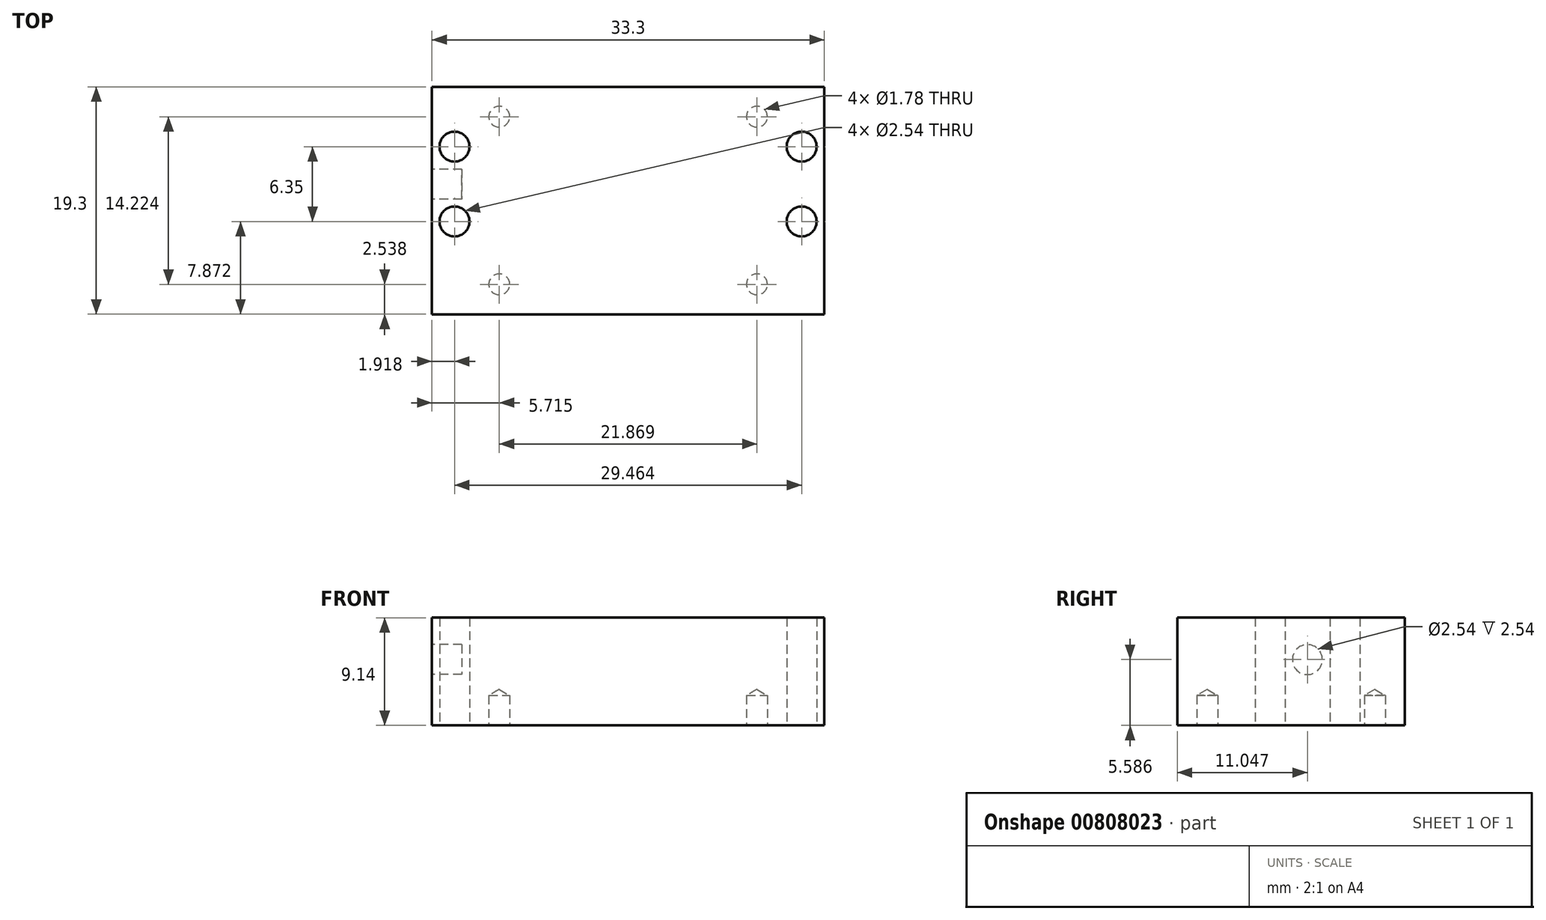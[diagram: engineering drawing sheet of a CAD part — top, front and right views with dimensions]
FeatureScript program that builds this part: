
annotation { "Feature Type Name" : "Feature", "Feature Type Description" : "" }
export const myFeature = defineFeature(function(context is Context, id is Id, definition is map)
    precondition{}
    {
        {
            var Q0;
            Q0=qCreatedBy(makeId("Top.planeOp"),FACE);
            var sketch = newSketch(context, id + "F0", { "sketchPlane" : qUnion([Q0])});
            skLineSegment(sketch, "E0.bottom", {"start": v(-16.65, 9.65) * mm, "end": v(16.65, 9.65) * mm});
            skLineSegment(sketch, "E0.top", {"start": v(-16.65, -9.65) * mm, "end": v(16.65, -9.65) * mm});
            skLineSegment(sketch, "E0.left", {"start": v(-16.65, 9.65) * mm, "end": v(-16.65, -9.65) * mm});
            skLineSegment(sketch, "E0.right", {"start": v(16.65, 9.65) * mm, "end": v(16.65, -9.65) * mm});
            skLineSegment(sketch, "E1", {"start": v(16.65, 9.65) * mm, "end": v(-16.65, -9.65) * mm, "construction": true});
            skSolve(sketch);
        }
        {
            var Q0;
            Q0 = qSketchRegion(id + "F0", true);
            extrude(context, id + "F1", {"entities" : qUnion([Q0]), "endBound" : BoundingType.SYMMETRIC, "depth" : 9.14 * mm, "offsetDistance" : 25.4 * mm});
        }
        {
            var Q0;
            Q0=makeQuery(id+"F1.opExtrude","SWEPT_FACE",FACE,{"disambiguationData":[OSD([sQuery(id+"F0.wireOp",EDGE,"E0.left")])]});
            var sketch = newSketch(context, id + "F2", { "sketchPlane" : qUnion([Q0])});
            skCircle(sketch, "E2", {"center": v(-1.4, 1.02) * mm, "radius": 1.27 * mm});
            skSolve(sketch);
        }
        {
            var Q0;
            Q0 = qSketchRegion(id + "F2", true);
            extrude(context, id + "F3", {"entities" : qUnion([Q0]), "operationType" : NewBodyOperationType.REMOVE, "oppositeDirection" : true, "depth" : 2.54 * mm, "offsetDistance" : 25.4 * mm});
        }
        {
            var Q0;
            Q0=makeQuery(id+"F1.opExtrude","CAP_FACE",FACE,{"disambiguationData":[OSD([sQuery(id+"F0.wireOp",EDGE,"E0.bottom"),sQuery(id+"F0.wireOp",EDGE,"E0.top"),sQuery(id+"F0.wireOp",EDGE,"E0.left"),sQuery(id+"F0.wireOp",EDGE,"E0.right")])],"isStart":true});
            var sketch = newSketch(context, id + "F4", { "sketchPlane" : qUnion([Q0])});
            skPoint(sketch, "E3", {"position": v(10.93, -7.11) * mm});
            skPoint(sketch, "E4", {"position": v(10.93, 7.11) * mm});
            skLineSegment(sketch, "E5", {"start": v(0, -9.65) * mm, "end": v(0, 9.65) * mm, "construction": true});
            skPoint(sketch, "E6.MirrorP", {"position": v(-10.93, -7.11) * mm});
            skPoint(sketch, "E7.MirrorP", {"position": v(-10.93, 7.11) * mm});
            skSolve(sketch);
        }
        {
            var Q0;
            Q0=sQuery(id+"F4.wireOp",VERTEX,"E3");
            var Q1;
            Q1=sQuery(id+"F4.wireOp",VERTEX,"E4");
            var Q2;
            Q2=sQuery(id+"F4.wireOp",VERTEX,"E6.MirrorP");
            var Q3;
            Q3=sQuery(id+"F4.wireOp",VERTEX,"E7.MirrorP");
            var Q4;
            Q4=makeQuery(id+"F1.opExtrude","SWEPT_BODY",BODY,{"disambiguationData":[OSD([sQuery(id+"F0.wireOp",EDGE,"E0.bottom"),sQuery(id+"F0.wireOp",EDGE,"E0.top"),sQuery(id+"F0.wireOp",EDGE,"E0.left"),sQuery(id+"F0.wireOp",EDGE,"E0.right")])]});
            hole(context, id + "F5", {"style" : HoleStyle.SIMPLE, "endStyle" : HoleEndStyle.BLIND, "standardTappedOrClearance" : lookupTablePath({ "standard" : "ANSI", "engagement" : "75%", "pitch" : "56 tpi", "size" : "#2", "type" : "Tapped" }), "standardBlindInLast" : lookupTablePath({ "standard" : "ANSI", "engagement" : "75%", "pitch" : "56 tpi", "size" : "#2", "type" : "Tapped" }), "holeDiameter" : 1.78 * mm, "majorDiameter" : 2.18 * mm, "showTappedDepth" : true, "holeDepth" : 2.54 * mm, "tappedDepth" : 1.18 * mm, "tapClearance" : 3, "locations" : qUnion([Q0, Q1, Q2, Q3]), "scope" : qUnion([Q4])});
        }
        {
            var Q0;
            Q0=makeQuery(id+"F1.opExtrude","SWEPT_FACE",FACE,{"disambiguationData":[OSD([sQuery(id+"F0.wireOp",EDGE,"E0.top")])]});
            var sketch = newSketch(context, id + "F6", { "sketchPlane" : qUnion([Q0])});
            skCircle(sketch, "E8", {"center": v(-3.19, -2.16) * mm, "radius": 0.64 * mm});
            skSolve(sketch);
        }
        {
            var Q0;
            Q0=makeQuery(id+"F1.opExtrude","SWEPT_FACE",FACE,{"disambiguationData":[OSD([sQuery(id+"F0.wireOp",EDGE,"E0.top")])]});
            var sketch = newSketch(context, id + "F7", { "sketchPlane" : qUnion([Q0])});
            skCircle(sketch, "E9", {"center": v(3.92, 1.27) * mm, "radius": 0.38 * mm});
            skSolve(sketch);
        }
        {
            var Q0;
            Q0=makeQuery(id+"F1.opExtrude","CAP_FACE",FACE,{"disambiguationData":[OSD([sQuery(id+"F0.wireOp",EDGE,"E0.bottom"),sQuery(id+"F0.wireOp",EDGE,"E0.top"),sQuery(id+"F0.wireOp",EDGE,"E0.left"),sQuery(id+"F0.wireOp",EDGE,"E0.right")])],"isStart":true});
            var sketch = newSketch(context, id + "F8", { "sketchPlane" : qUnion([Q0])});
            skPoint(sketch, "E10", {"position": v(-14.73, 1.78) * mm});
            skPoint(sketch, "E11", {"position": v(-14.73, -4.57) * mm});
            skLineSegment(sketch, "E12", {"start": v(0, 0) * mm, "end": v(0, 9.65) * mm, "construction": true});
            skCircle(sketch, "E13", {"center": v(-14.73, 1.78) * mm, "radius": 1.27 * mm});
            skCircle(sketch, "E14", {"center": v(-14.73, -4.57) * mm, "radius": 1.27 * mm});
            skCircle(sketch, "E15.MirrorC", {"center": v(14.73, 1.78) * mm, "radius": 1.27 * mm});
            skCircle(sketch, "E16.MirrorC", {"center": v(14.73, -4.57) * mm, "radius": 1.27 * mm});
            skSolve(sketch);
        }
        {
            var Q0;
            Q0 = qSketchRegion(id + "F8", true);
            extrude(context, id + "F9", {"entities" : qUnion([Q0]), "operationType" : NewBodyOperationType.REMOVE, "endBound" : BoundingType.THROUGH_ALL, "oppositeDirection" : true, "depth" : 25.4 * mm, "offsetDistance" : 25.4 * mm});
        }
    });
